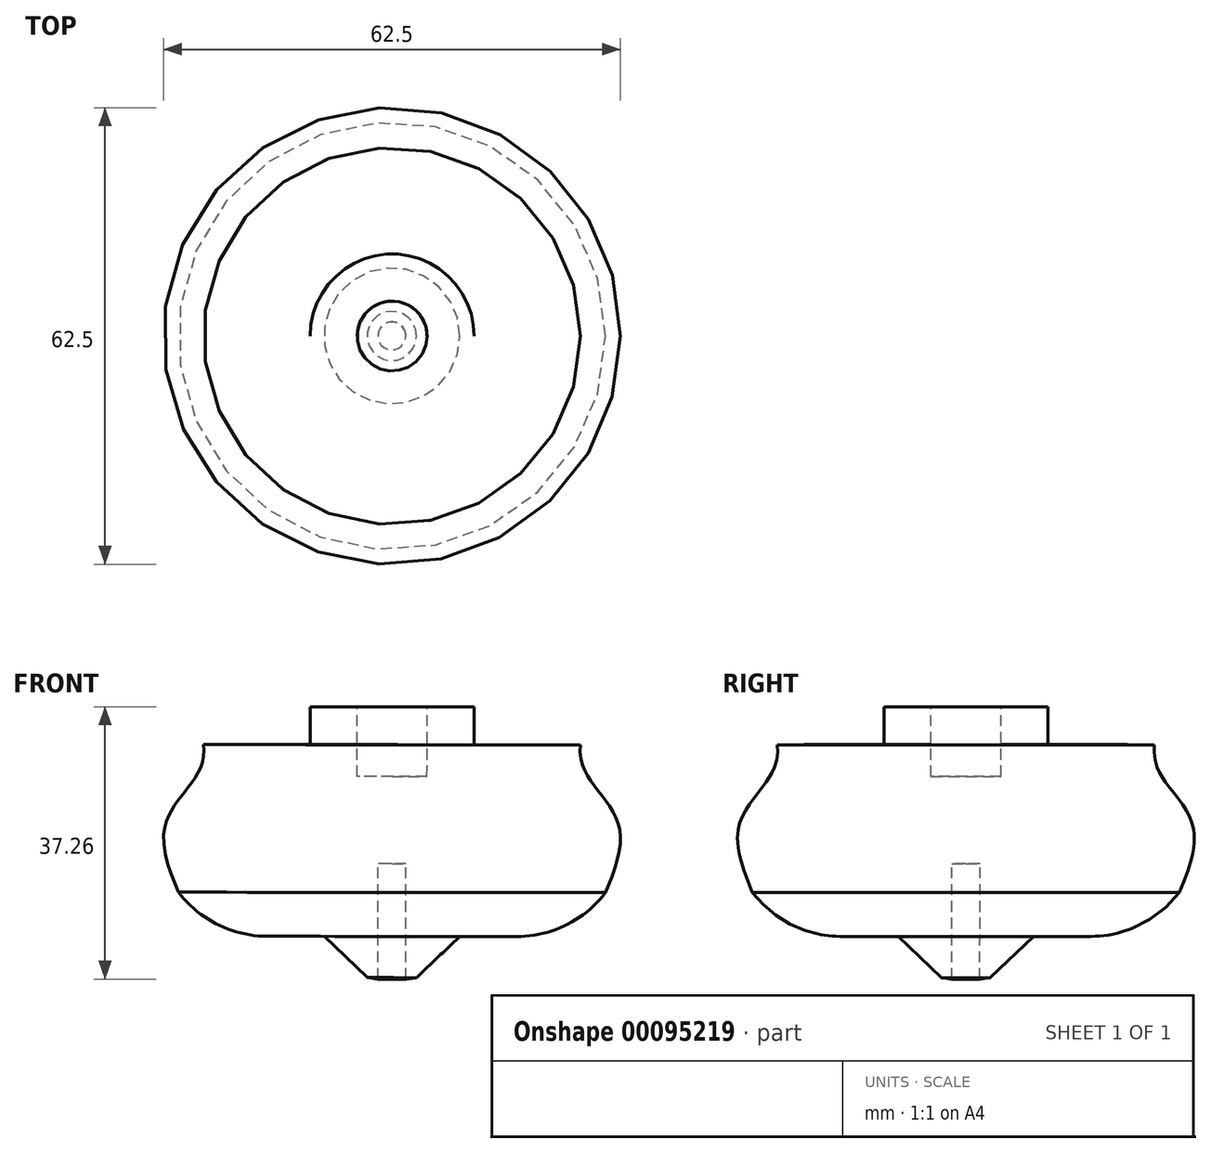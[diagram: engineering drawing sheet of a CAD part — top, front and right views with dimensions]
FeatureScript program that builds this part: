
annotation { "Feature Type Name" : "Feature", "Feature Type Description" : "" }
export const myFeature = defineFeature(function(context is Context, id is Id, definition is map)
    precondition{}
    {
        {
            var Q0;
            Q0=qCreatedBy(makeId("Front.planeOp"),FACE);
            var sketch = newSketch(context, id + "F0", { "sketchPlane" : qUnion([Q0])});
            skLineSegment(sketch, "E0", {"start": v(-4.3, 5.17) * mm, "end": v(-10.73, 5.17) * mm});
            skLineSegment(sketch, "E1", {"start": v(-10.73, 5.17) * mm, "end": v(-10.73, 0) * mm});
            skLineSegment(sketch, "E2", {"start": v(-10.73, 0) * mm, "end": v(-25.3, 0) * mm});
            skLineSegment(sketch, "E3", {"start": v(-16.57, -26.23) * mm, "end": v(-8.84, -26.23) * mm});
            skLineSegment(sketch, "E4", {"start": v(0.48, -4.4) * mm, "end": v(-4.3, -4.35) * mm});
            skLineSegment(sketch, "E5", {"start": v(-4.3, -4.35) * mm, "end": v(-4.3, 5.17) * mm});
            skPoint(sketch, "E6.orphan", {"position": v(0, 5.17) * mm});
            skPoint(sketch, "E7.end.orphan", {"position": v(0, -32.29) * mm});
            skLineSegment(sketch, "E8", {"start": v(-8.84, -26.23) * mm, "end": v(-2.93, -31.89) * mm});
            skLineSegment(sketch, "E9", {"start": v(-2.93, -31.89) * mm, "end": v(-1.46, -32.09) * mm});
            skLineSegment(sketch, "E10", {"start": v(-1.46, -32.09) * mm, "end": v(-1.46, -15.04) * mm});
            skPoint(sketch, "E10.endSnap0", {"position": v(-1.46, -32.09) * mm});
            skLineSegment(sketch, "E11", {"start": v(-1.02, -16.3) * mm, "end": v(0.46, -16.3) * mm});
            skFitSpline(sketch, "E12", {"points": [v(-25.3, 0) * mm, v(-30.77, -12.45) * mm, v(-26.51, -26.23) * mm], "startDerivative": vector(4.1, -31.39) * mm, "endDerivative": vector(-7.6, 0) * mm});
            skLineSegment(sketch, "E13", {"start": v(0.48, -4.4) * mm, "end": v(0.46, -16.3) * mm});
            skArc(sketch, "E14", {"start": v(-28.75, -20.2) * mm, "mid": v(-23.37, -24.64) * mm, "end": v(-16.57, -26.23) * mm});
            skLineSegment(sketch, "E15", {"start": v(-1.46, -16.3) * mm, "end": v(0.46, -16.3) * mm});
            skSolve(sketch);
        }
        {
            var Q0;
            Q0=makeQuery(id+"F0.imprint","IMPRINT",FACE,{"disambiguationData":[TD([[makeQuery(id+"F0.imprint","IMPRINT",EDGE,{"derivedFrom":sQuery(id+"F0.wireOp",EDGE,"E0")}),1.0]])]});
            var Q1;
            Q1=sQuery(id+"F0.wireOp",EDGE,"E13");
            revolve(context, id + "F1", {"entities" : qUnion([Q0]), "axis" : qUnion([Q1]), "revolveType" : RevolveType.FULL});
        }
    });
